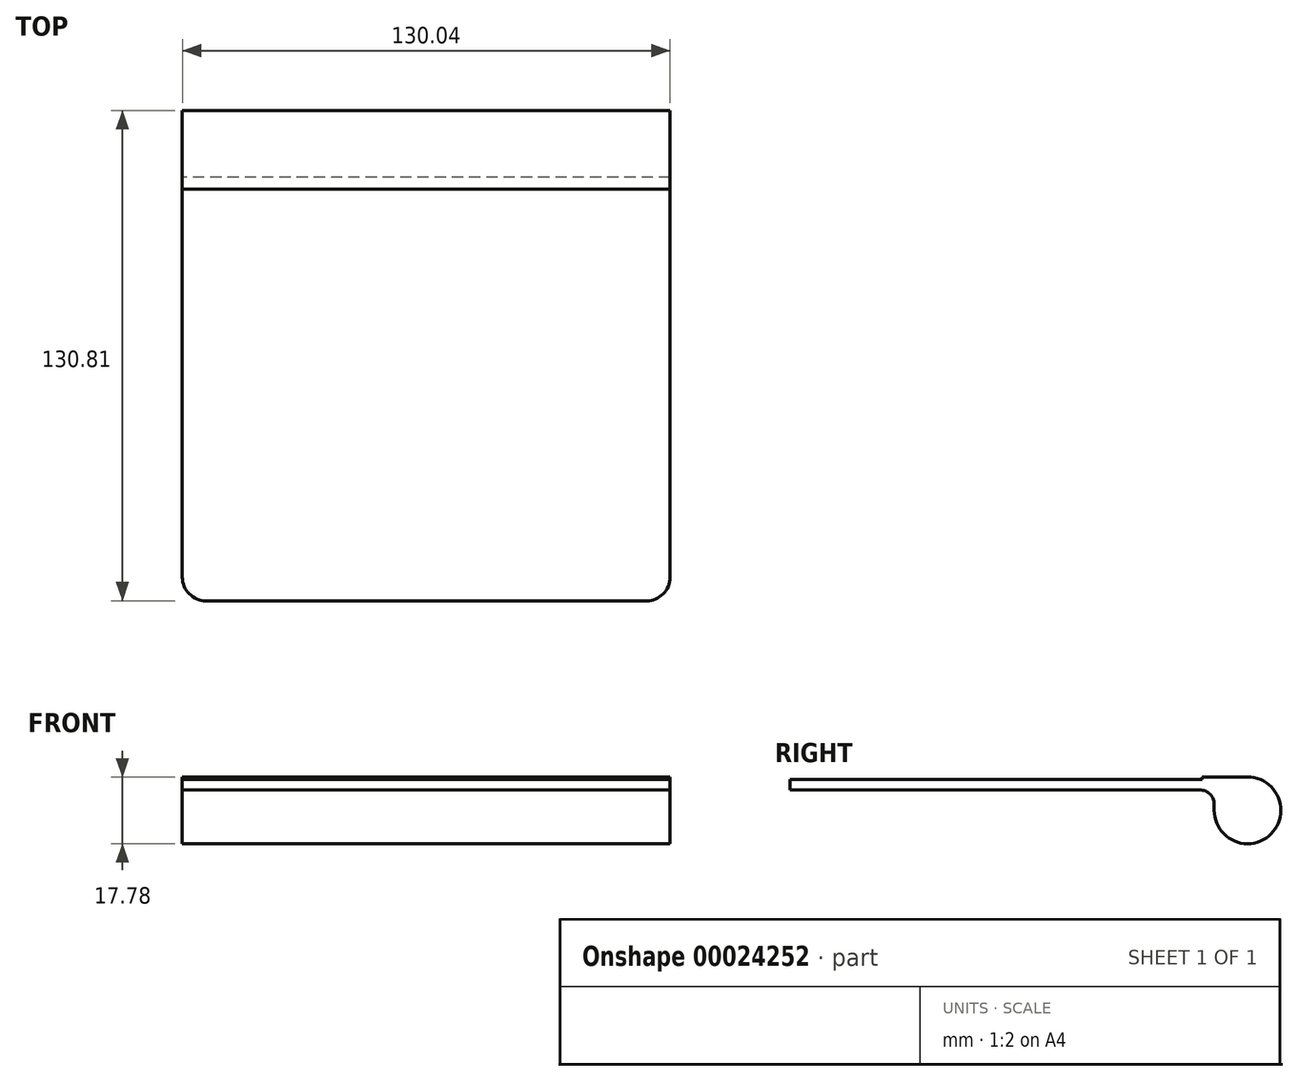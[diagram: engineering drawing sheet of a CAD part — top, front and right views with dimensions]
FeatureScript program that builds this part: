
annotation { "Feature Type Name" : "Feature", "Feature Type Description" : "" }
export const myFeature = defineFeature(function(context is Context, id is Id, definition is map)
    precondition{}
    {
        {
            var Q0;
            Q0=qCreatedBy(makeId("Right.planeOp"),FACE);
            var sketch = newSketch(context, id + "F0", { "sketchPlane" : qUnion([Q0])});
            skArc(sketch, "E0", {"start": v(-8.9, -8.9) * mm, "mid": v(6.29, -15.18) * mm, "end": v(0, 0) * mm});
            skLineSegment(sketch, "E1.bottom", {"start": v(0, 0) * mm, "end": v(-121.92, 0) * mm});
            skLineSegment(sketch, "E1.top", {"start": v(-12.7, -3.43) * mm, "end": v(-121.92, -3.43) * mm});
            skLineSegment(sketch, "E1.right", {"start": v(-121.92, 0) * mm, "end": v(-121.92, -3.43) * mm});
            skLineSegment(sketch, "E2", {"start": v(-8.9, -8.9) * mm, "end": v(-8.9, -7.24) * mm});
            skPoint(sketch, "E3.visualSharp", {"position": v(-8.9, -3.43) * mm});
            skArc(sketch, "E3.filletArc", {"start": v(-8.89, -7.24) * mm, "mid": v(-10, -4.54) * mm, "end": v(-12.7, -3.43) * mm});
            skSolve(sketch);
        }
        {
            var Q0;
            Q0 = qSketchRegion(id + "F0", true);
            extrude(context, id + "F1", {"entities" : qUnion([Q0]), "endBound" : BoundingType.SYMMETRIC, "depth" : 130.05 * mm});
        }
        {
            var Q0;
            Q0=makeQuery(id+"F1.opExtrude","CAP_EDGE",EDGE,{"disambiguationData":[OSD([sQuery(id+"F0.wireOp",EDGE,"E1.right")])],"isStart":true});
            var Q1;
            Q1=makeQuery(id+"F1.opExtrude","CAP_EDGE",EDGE,{"disambiguationData":[OSD([sQuery(id+"F0.wireOp",EDGE,"E1.right")])],"isStart":false});
            fillet(context, id + "F2", {"entities" : qUnion([Q0, Q1]), "radius" : 6.35 * mm, "tangentPropagation" : true, "allowEdgeOverflow" : false});
        }
        {
            var Q0;
            Q0=qCreatedBy(makeId("Right.planeOp"),FACE);
            var sketch = newSketch(context, id + "F3", { "sketchPlane" : qUnion([Q0])});
            skLineSegment(sketch, "E4.bottom", {"start": v(-12.07, 0) * mm, "end": v(-121.92, 0) * mm});
            skLineSegment(sketch, "E4.top", {"start": v(-12.06, -0.63) * mm, "end": v(-121.92, -0.64) * mm});
            skLineSegment(sketch, "E4.left", {"start": v(-12.06, 0) * mm, "end": v(-12.06, -0.63) * mm});
            skLineSegment(sketch, "E4.right", {"start": v(-121.92, 0) * mm, "end": v(-121.92, -0.64) * mm});
            skSolve(sketch);
        }
        {
            var Q0;
            Q0 = qSketchRegion(id + "F3", true);
            extrude(context, id + "F4", {"entities" : qUnion([Q0]), "operationType" : NewBodyOperationType.REMOVE, "endBound" : BoundingType.SYMMETRIC, "oppositeDirection" : true, "depth" : 152.4 * mm});
        }
    });
